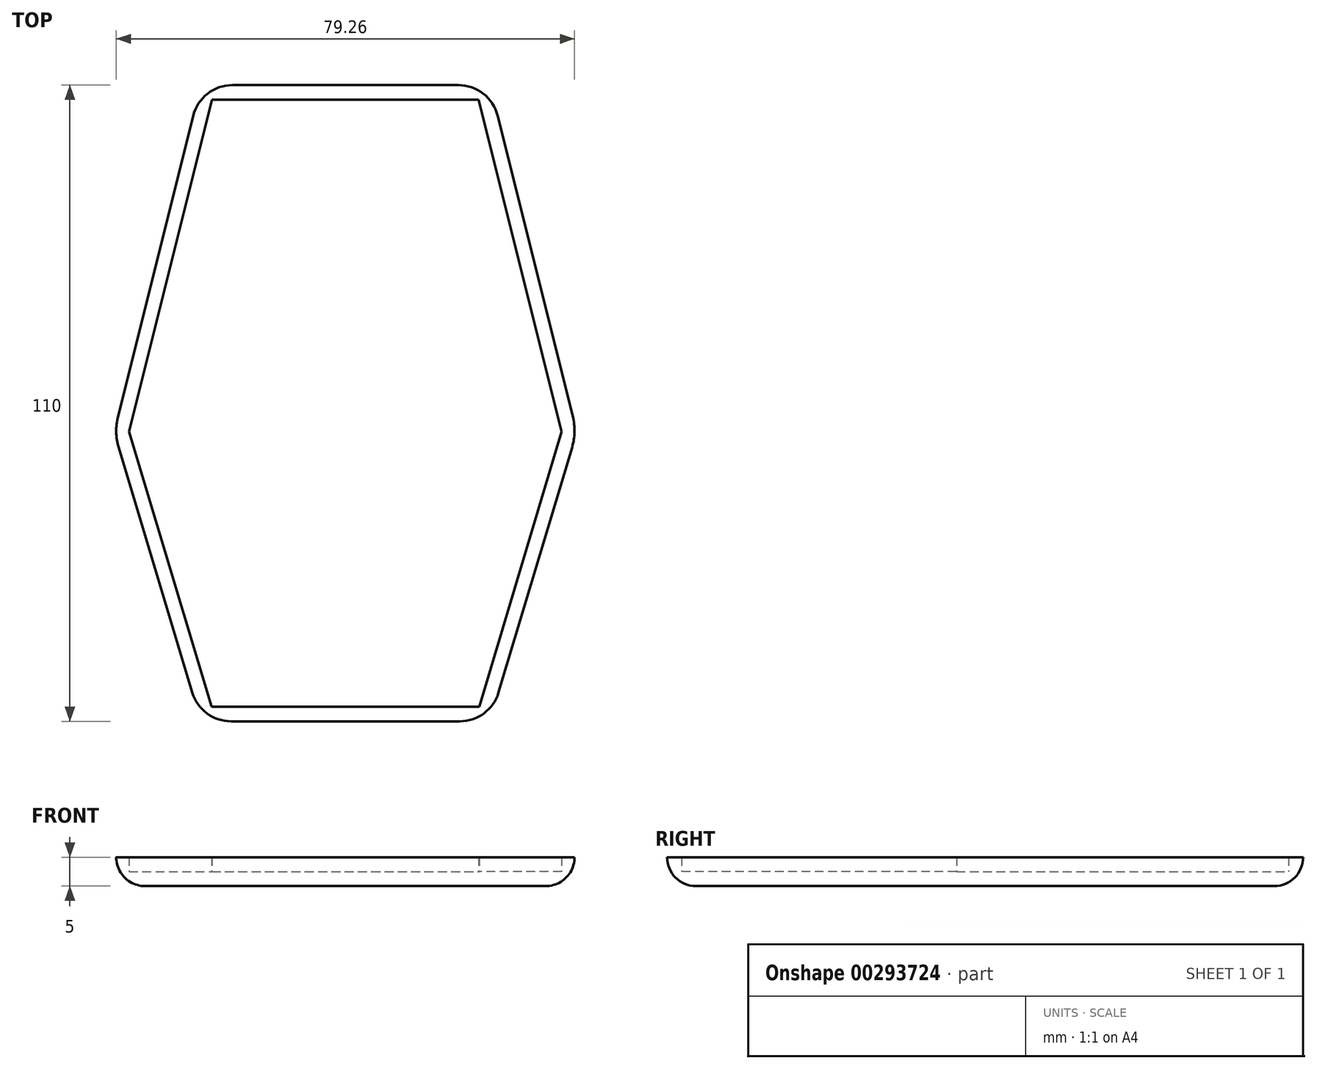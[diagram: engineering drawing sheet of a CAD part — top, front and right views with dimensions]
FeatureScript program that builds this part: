
annotation { "Feature Type Name" : "Feature", "Feature Type Description" : "" }
export const myFeature = defineFeature(function(context is Context, id is Id, definition is map)
    precondition{}
    {
        {
            var Q0;
            Q0=qCreatedBy(makeId("Top.planeOp"),FACE);
            var sketch = newSketch(context, id + "F0", { "sketchPlane" : qUnion([Q0])});
            skLineSegment(sketch, "E0.bottom", {"start": v(-25, 55) * mm, "end": v(25, 55) * mm});
            skLineSegment(sketch, "E0.top", {"start": v(-25, -55) * mm, "end": v(25, -55) * mm});
            skPoint(sketch, "E0.middle", {"position": v(0, 0) * mm});
            skLineSegment(sketch, "E1", {"start": v(-40, -5) * mm, "end": v(-25, 55) * mm});
            skLineSegment(sketch, "E2", {"start": v(-40, -5) * mm, "end": v(-25, -55) * mm});
            skPoint(sketch, "E3.orphan", {"position": v(-40, 55) * mm});
            skPoint(sketch, "E4.orphan", {"position": v(-40, -55) * mm});
            skLineSegment(sketch, "E5.MirrorCS", {"start": v(40, -5) * mm, "end": v(25, 55) * mm});
            skPoint(sketch, "E6.MirrorP", {"position": v(40, -55) * mm});
            skPoint(sketch, "E7.MirrorP", {"position": v(40, 55) * mm});
            skLineSegment(sketch, "E8.MirrorCS", {"start": v(40, -5) * mm, "end": v(25, -55) * mm});
            skSolve(sketch);
        }
        {
            var Q0;
            Q0 = qSketchRegion(id + "F0", true);
            extrude(context, id + "F1", {"entities" : qUnion([Q0]), "depth" : 5 * mm});
        }
        {
            var Q0;
            Q0=makeQuery(id+"F1.opExtrude","CAP_FACE",FACE,{"disambiguationData":[OSD([sQuery(id+"F0.wireOp",EDGE,"E0.bottom"),sQuery(id+"F0.wireOp",EDGE,"E0.top"),sQuery(id+"F0.wireOp",EDGE,"E1"),sQuery(id+"F0.wireOp",EDGE,"E2"),sQuery(id+"F0.wireOp",EDGE,"E5.MirrorCS"),sQuery(id+"F0.wireOp",EDGE,"E8.MirrorCS")])],"isStart":false});
            shell(context, id + "F2", {"entities" : qUnion([Q0]), "thickness" : 2.5 * mm});
        }
        {
            var Q0;
            Q0=makeQuery(id+"F1.opExtrude","SWEPT_EDGE",EDGE,{"disambiguationData":[OSD([sQuery(id+"F0.wireOp",EDGE,"E0.bottom"),sQuery(id+"F0.wireOp",EDGE,"E5.MirrorCS")])]});
            fillet(context, id + "F3", {"entities" : qUnion([Q0]), "radius" : 7 * mm, "tangentPropagation" : true, "allowEdgeOverflow" : false});
        }
        {
            var Q0;
            Q0=makeQuery(id+"F1.opExtrude","SWEPT_EDGE",EDGE,{"disambiguationData":[OSD([sQuery(id+"F0.wireOp",EDGE,"E0.bottom"),sQuery(id+"F0.wireOp",EDGE,"E1")])]});
            fillet(context, id + "F4", {"entities" : qUnion([Q0]), "radius" : 7 * mm, "tangentPropagation" : true, "allowEdgeOverflow" : false});
        }
        {
            var Q0;
            Q0=makeQuery(id+"F1.opExtrude","SWEPT_EDGE",EDGE,{"disambiguationData":[OSD([sQuery(id+"F0.wireOp",EDGE,"E1"),sQuery(id+"F0.wireOp",EDGE,"E2")])]});
            fillet(context, id + "F5", {"entities" : qUnion([Q0]), "radius" : 10 * mm, "tangentPropagation" : true, "allowEdgeOverflow" : false});
        }
        {
            var Q0;
            Q0=makeQuery(id+"F1.opExtrude","SWEPT_EDGE",EDGE,{"disambiguationData":[OSD([sQuery(id+"F0.wireOp",EDGE,"E5.MirrorCS"),sQuery(id+"F0.wireOp",EDGE,"E8.MirrorCS")])]});
            fillet(context, id + "F6", {"entities" : qUnion([Q0]), "radius" : 10 * mm, "tangentPropagation" : true, "allowEdgeOverflow" : false});
        }
        {
            var Q0;
            Q0=makeQuery(id+"F1.opExtrude","SWEPT_EDGE",EDGE,{"disambiguationData":[OSD([sQuery(id+"F0.wireOp",EDGE,"E0.top"),sQuery(id+"F0.wireOp",EDGE,"E2")])]});
            fillet(context, id + "F7", {"entities" : qUnion([Q0]), "radius" : 7 * mm, "tangentPropagation" : true, "allowEdgeOverflow" : false});
        }
        {
            var Q0;
            Q0=makeQuery(id+"F1.opExtrude","SWEPT_EDGE",EDGE,{"disambiguationData":[OSD([sQuery(id+"F0.wireOp",EDGE,"E0.top"),sQuery(id+"F0.wireOp",EDGE,"E8.MirrorCS")])]});
            fillet(context, id + "F8", {"entities" : qUnion([Q0]), "radius" : 7 * mm, "tangentPropagation" : true, "allowEdgeOverflow" : false});
        }
        {
            var Q0;
            Q0=makeQuery(id+"F1.opExtrude","CAP_EDGE",EDGE,{"disambiguationData":[OSD([sQuery(id+"F0.wireOp",EDGE,"E8.MirrorCS")])],"isStart":true});
            fillet(context, id + "F9", {"entities" : qUnion([Q0]), "radius" : 5 * mm, "tangentPropagation" : true, "allowEdgeOverflow" : false});
        }
    });
